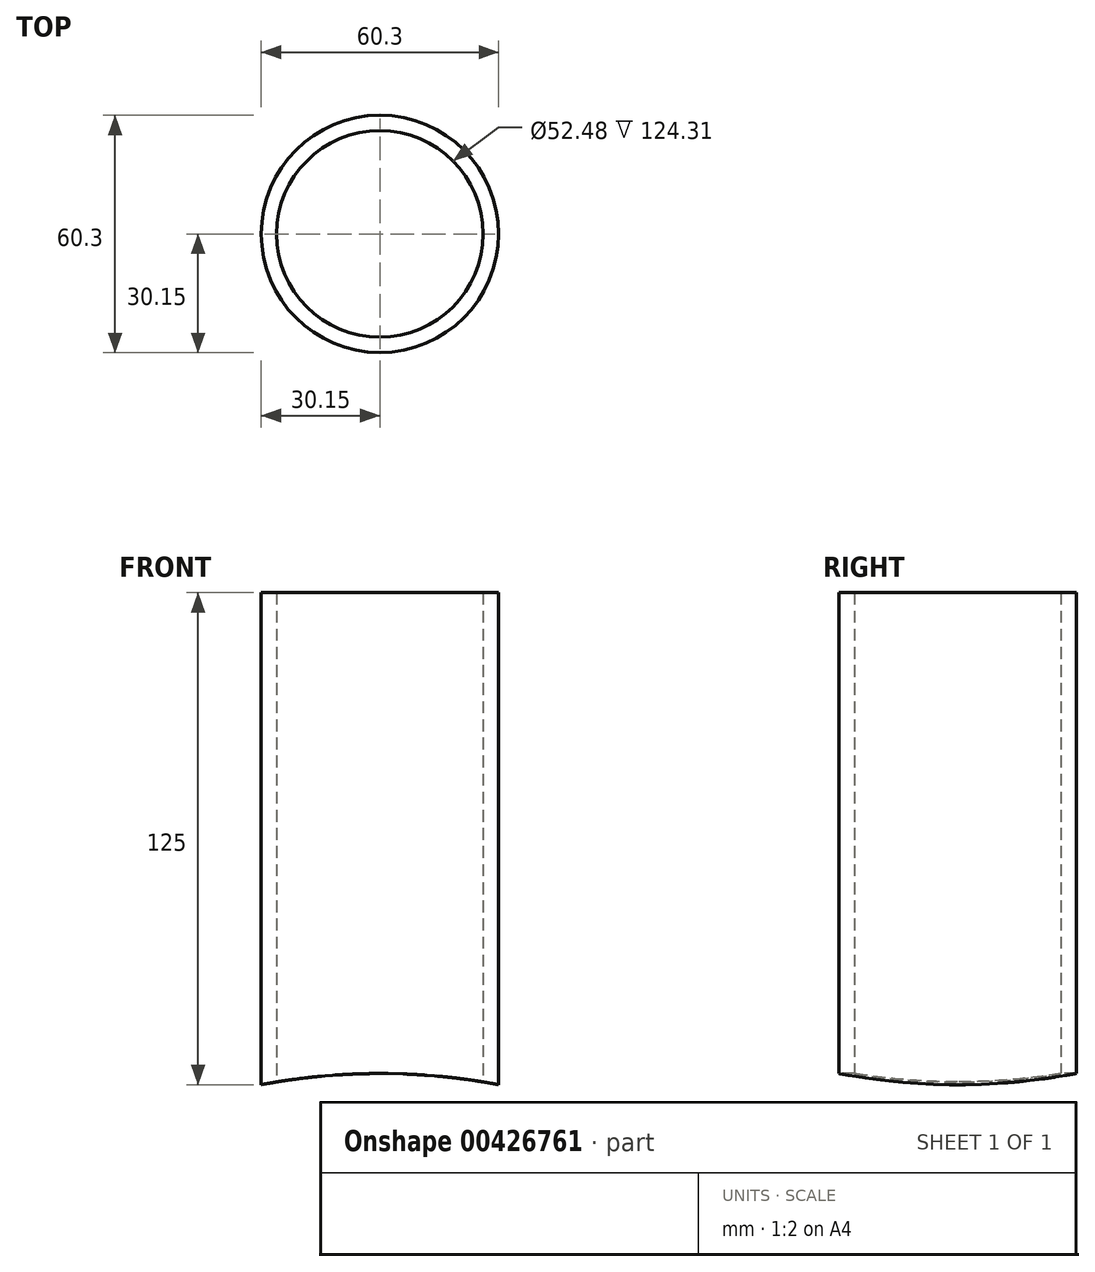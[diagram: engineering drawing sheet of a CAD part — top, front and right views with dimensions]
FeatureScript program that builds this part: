
annotation { "Feature Type Name" : "Feature", "Feature Type Description" : "" }
export const myFeature = defineFeature(function(context is Context, id is Id, definition is map)
    precondition{}
    {
        {
            var Q0;
            Q0=qCreatedBy(makeId("Top.planeOp"),FACE);
            var sketch = newSketch(context, id + "F0", { "sketchPlane" : qUnion([Q0])});
            skCircle(sketch, "E0", {"center": v(0, 0) * mm, "radius": 30.15 * mm});
            skCircle(sketch, "E1.0", {"center": v(0, 0) * mm, "radius": 26.24 * mm});
            skSolve(sketch);
        }
        {
            var Q0;
            Q0=makeQuery(id+"F0.imprint","IMPRINT",FACE,{"disambiguationData":[TD([[makeQuery(id+"F0.imprint","IMPRINT",EDGE,{"derivedFrom":sQuery(id+"F0.wireOp",EDGE,"E0")}),1.0]])]});
            extrude(context, id + "F1", {"entities" : qUnion([Q0]), "depth" : 125 * mm});
        }
        {
            var Q0;
            Q0=qCreatedBy(makeId("Front.planeOp"),FACE);
            var sketch = newSketch(context, id + "F2", { "sketchPlane" : qUnion([Q0])});
            skLineSegment(sketch, "E2.0", {"start": v(-30.15, 0) * mm, "end": v(30.15, 0) * mm});
            skCircle(sketch, "E3", {"center": v(0, -159.17) * mm, "radius": 162 * mm});
            skPoint(sketch, "E3.third.point", {"position": v(-158.5, -125.7) * mm});
            skSolve(sketch);
        }
        {
            var Q0;
            {var subQ0=sQuery(id+"F2.wireOp",EDGE,"E2.0");Q0=makeQuery(id+"F2.imprint","IMPRINT",FACE,{"disambiguationData":[TD([[makeQuery(id+"F2.imprint","IMPRINT",EDGE,{"derivedFrom":subQ0}),1.0]])]});}
            extrude(context, id + "F3", {"entities" : qUnion([Q0]), "operationType" : NewBodyOperationType.REMOVE, "endBound" : BoundingType.SYMMETRIC, "oppositeDirection" : true, "depth" : 100 * mm});
        }
    });
